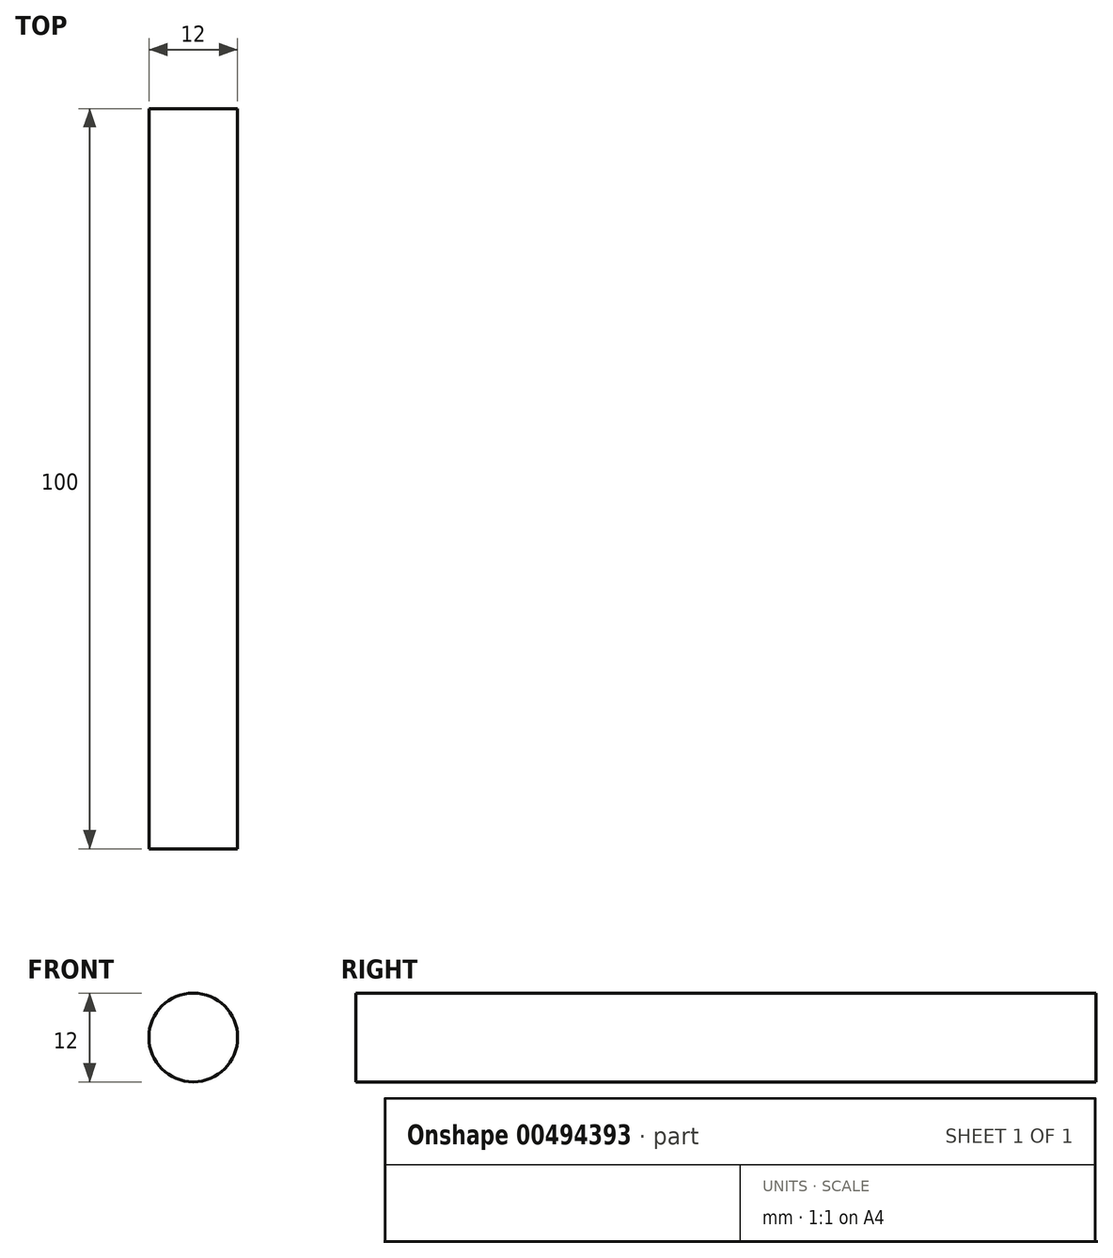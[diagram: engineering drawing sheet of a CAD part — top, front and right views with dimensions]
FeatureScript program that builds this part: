
annotation { "Feature Type Name" : "Feature", "Feature Type Description" : "" }
export const myFeature = defineFeature(function(context is Context, id is Id, definition is map)
    precondition{}
    {
        {
            var Q0;
            Q0=qCreatedBy(makeId("Front.planeOp"),FACE);
            var sketch = newSketch(context, id + "F0", { "sketchPlane" : qUnion([Q0])});
            skCircle(sketch, "E0", {"center": v(0, 0) * mm, "radius": 6 * mm});
            skSolve(sketch);
        }
        {
            var Q0;
            Q0 = qSketchRegion(id + "F0", true);
            extrude(context, id + "F1", {"entities" : qUnion([Q0]), "depth" : 100 * mm});
        }
    });
